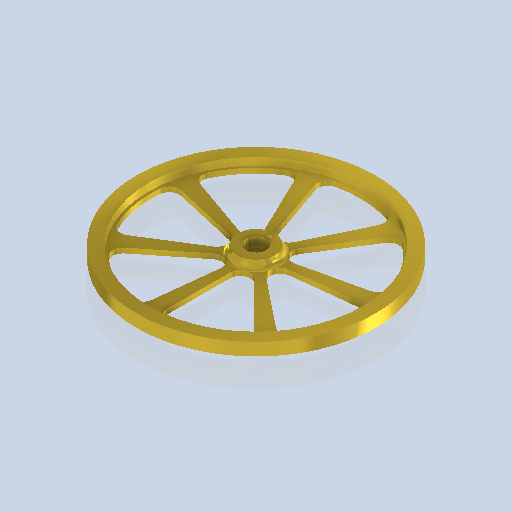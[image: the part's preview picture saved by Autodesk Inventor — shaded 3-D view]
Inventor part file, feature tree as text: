
AUTODESK INVENTOR PART (.ipt)
format: ipt  version: 2024.2 (Build 282272000, 272)  size: 410,624 bytes
history: native  units: mm
features: sketch x7, extrude x5, hole x2, pattern_circular x1, fillet x1
ambient origin geometry x8: Origin, YZ Plane, XZ Plane, XY Plane, X Axis, Y Axis, Z Axis, Center Point
bodies: Volumenkörper1 (feature_tree)
feature tree (16):
  extrude  "Extrusion1"  Depth=5.0mm TaperAngle=0.0deg
  extrude  "Extrusion4"  Depth=3.0mm TaperAngle=0.0deg
  extrude  "Extrusion6"  Depth=2.0mm TaperAngle=0.0deg
  hole  "Bohrung2"  [1 undecoded]
  extrude  "Extrusion7"  Depth=83.0mm
  extrude  "Extrusion8"  Depth=1.5mm
  pattern_circular  "Runde Anordnung1"  [2 undecoded]
  fillet  "Rundung1"  Radius=41.5mm
  hole  "Bohrung3"  [1 undecoded]
  sketch  "Skizze1"  dims[d0=95.0mm d1=5.0mm d2=0.0mm]
  sketch  "Skizze6"  dims[d18=85.0mm d19=3.0mm d20=0.0mm]
  sketch  "Skizze8"  dims[d24=15.0mm d25=2.0mm d26=0.0mm]
  sketch  "Skizze9"  dims[d27=3.0mm d28=6.0mm d29=8.0mm d30=4.0mm d31=90.0deg d32=8.0mm d33=20.594885mm d34=5.0mm]
  sketch  "Skizze10"  dims[d35=3.0mm d36=0.0mm d37=83.0mm]
  sketch  "Skizze11"  dims[d38=17.352mm d39=1.5mm]
  sketch  "Skizze12"  dims[d40=45.0deg d41=4.0mm d42=41.5mm d43=25.0mm d44=4.0mm d45=3.0mm d46=0.0mm d47=70.0mm d48=360.0deg d50=2.0mm d51=1.6mm d52=6.0mm d53=8.0mm d54=4.0mm d55=90.0deg d56=8.0mm d57=20.594885mm d58=5.5mm]
note: 4 required parameter values undecoded (feature->parameter linkage not recoverable at this tier; creation-order binding heuristic only, values carry confidence <= 0.55)
